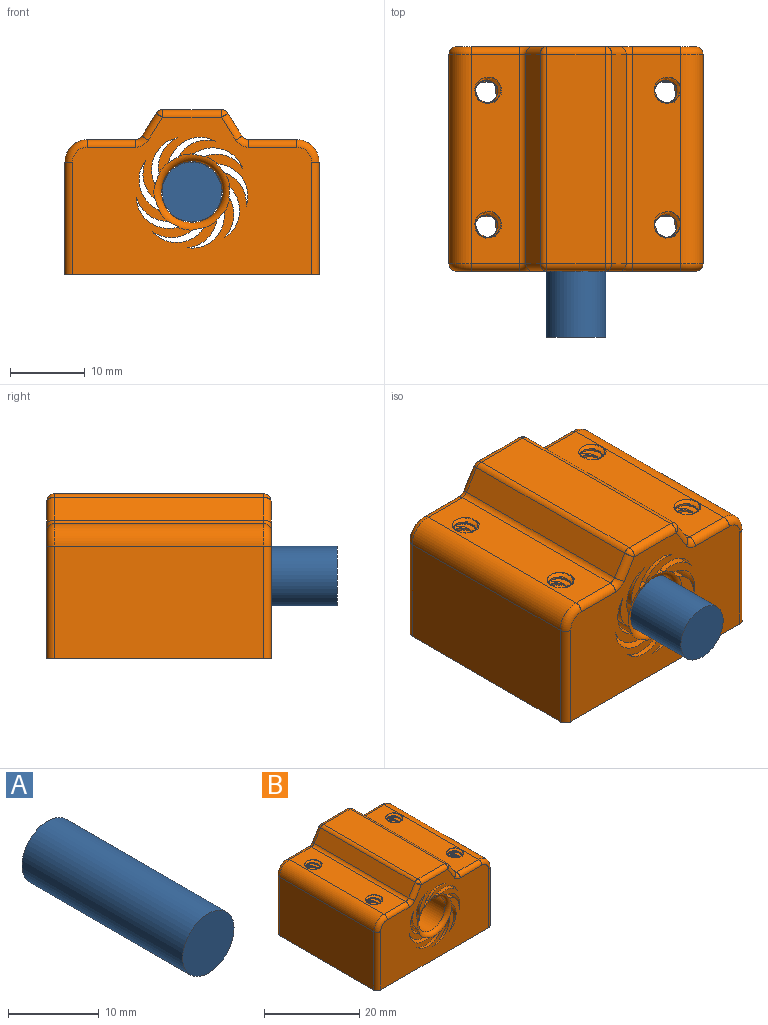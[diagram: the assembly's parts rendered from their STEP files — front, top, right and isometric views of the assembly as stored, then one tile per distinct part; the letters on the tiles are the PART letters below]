
ASSEMBLY  parts=2 mates=1
PART A: 3 faces, bbox 8x25x8 mm
  f0: cylinder r=4mm len=25mm, axis (0,1,0), area 628.3mm2, adj f1,f2
  f1: plane 8x8mm, normal (0,-1,0), area 50.3mm2, adj f0
  f2: plane 8x8mm, normal (0,1,0), area 50.3mm2, adj f0
PART B: 97 faces, bbox 34.8x30.3x22.7 mm
  f0: plane 32x21mm, normal (0,1,0), area 465.1mm2, adj f21,f28,f29,f31,f33,f36,f41,f42
  f1: plane 32x21mm, normal (0,-1,0), area 465.1mm2, adj f21,f30,f32,f34,f37,f39,f46,f52
  f2: plane 28x7.89mm, normal (0,0,1), area 221mm2, adj f40,f41,f46,f47
  f3: bspline ~18.65x4.71mm, area 125.6mm2, adj f5,f6,f21,f24
  f4: bspline ~18.81x4.71mm, area 125.4mm2, adj f5,f6,f21,f24
  f5: bspline ~18.46x4.82mm, area 33.9mm2, adj f3,f4,f21,f24
  f6: cylinder r=1.5mm len=18mm, axis (0,0,1), area 24.7mm2, adj f3,f4,f21,f24
  f7: bspline ~18.65x4.71mm, area 125.6mm2, adj f9,f10,f21,f24
  f8: bspline ~18.81x4.71mm, area 125.4mm2, adj f9,f10,f21,f24
  f9: bspline ~18.46x4.82mm, area 33.9mm2, adj f7,f8,f21,f24
  f10: cylinder r=1.5mm len=18mm, axis (0,0,1), area 24.7mm2, adj f7,f8,f21,f24
  f11: bspline ~18.65x4.71mm, area 125.6mm2, adj f13,f14,f21,f22
  f12: bspline ~18.81x4.71mm, area 125.4mm2, adj f13,f14,f21,f22
  f13: bspline ~18.46x4.82mm, area 33.9mm2, adj f11,f12,f21,f22
  f14: cylinder r=1.5mm len=18mm, axis (0,0,1), area 24.7mm2, adj f11,f12,f21,f22
  f15: bspline ~18.65x4.71mm, area 125.6mm2, adj f17,f18,f21,f22
  f16: bspline ~18.81x4.71mm, area 125.4mm2, adj f17,f18,f21,f22
  f17: bspline ~18.46x4.82mm, area 33.9mm2, adj f15,f16,f21,f22
  f18: cylinder r=1.5mm len=18mm, axis (0,0,1), area 24.7mm2, adj f15,f16,f21,f22
  f19: plane 28x15mm, normal (-1,0,0), area 420mm2, adj f21,f26,f28,f30
  f20: plane 28x15mm, normal (1,0,0), area 420mm2, adj f21,f27,f42,f55
  f21: plane 34.28x30.28mm, normal (0,0,-1), area 980.6mm2, adj f0,f1,f3,f4,f5,f6,f7,f8
  f22: plane 28.28x6.72mm, normal (0,0,1), area 161.2mm2, adj f11,f12,f13,f14,f15,f16,f17,f18
  f23: plane 28x3.06mm, normal (0.85,0,0.53), area 101mm2, adj f47,f48,f52,f53
  f24: plane 28.28x6.72mm, normal (0,0,1), area 161.2mm2, adj f3,f4,f5,f6,f7,f8,f9,f10
  f25: plane 28x3.06mm, normal (-0.85,0,0.53), area 101mm2, adj f35,f36,f39,f40
  f26: cylinder r=3mm len=28mm, axis (0,-1,0), area 131.9mm2, adj f19,f24,f29,f32
  f27: cylinder r=3mm len=28mm, axis (0,1,0), area 131.9mm2, adj f20,f22,f45,f57
  f28: cylinder r=1mm len=15mm, axis (0,0,-1), area 23.6mm2, adj f0,f19,f21,f29
  f29: torus R=2mm, axis (0,1,0), area 6.5mm2, adj f0,f26,f28,f31
  f30: cylinder r=1mm len=15mm, axis (0,0,1), area 23.6mm2, adj f1,f19,f21,f32
  f31: cylinder r=1mm len=6.45mm, axis (1,0,0), area 10.1mm2, adj f0,f24,f29,f33
  f32: torus R=2mm, axis (0,1,0), area 6.5mm2, adj f1,f26,f30,f34
  f33: torus R=2mm, axis (0,1,0), area 2.2mm2, adj f0,f31,f35,f36
  f34: cylinder r=1mm len=6.45mm, axis (1,0,0), area 10.1mm2, adj f1,f24,f32,f37
  f35: cylinder r=1mm len=28mm, axis (0,1,0), area 28.3mm2, adj f24,f25,f33,f37
  f36: cylinder r=1mm len=3.59mm, axis (0.53,0,0.85), area 5.7mm2, adj f0,f25,f33,f38
  f37: torus R=2mm, axis (0,1,0), area 2.2mm2, adj f1,f34,f35,f39
  f38: sphere r=1mm, area 1.1mm2, adj f36,f40,f41
  f39: cylinder r=1mm len=3.59mm, axis (0.53,0,0.85), area 5.7mm2, adj f1,f25,f37,f43
  f40: cylinder r=1mm len=28mm, axis (0,-1,0), area 28.3mm2, adj f2,f25,f38,f43
  f41: cylinder r=1mm len=7.89mm, axis (1,0,0), area 12.4mm2, adj f0,f2,f38,f44
  f42: cylinder r=1mm len=15mm, axis (0,0,1), area 23.6mm2, adj f0,f20,f21,f45
  f43: sphere r=1mm, area 1.1mm2, adj f39,f40,f46
  f44: sphere r=1mm, area 1.1mm2, adj f41,f47,f48
  f45: torus R=2mm, axis (0,1,0), area 6.5mm2, adj f0,f27,f42,f49
  f46: cylinder r=1mm len=7.89mm, axis (-1,0,0), area 12.4mm2, adj f1,f2,f43,f50
  f47: cylinder r=1mm len=28mm, axis (0,1,0), area 28.3mm2, adj f2,f23,f44,f50
  f48: cylinder r=1mm len=3.59mm, axis (0.53,0,-0.85), area 5.7mm2, adj f0,f23,f44,f51
  f49: cylinder r=1mm len=6.45mm, axis (1,0,0), area 10.1mm2, adj f0,f22,f45,f51
  f50: sphere r=1mm, area 1mm2, adj f46,f47,f52
  f51: torus R=2mm, axis (0,1,0), area 2.2mm2, adj f0,f48,f49,f53
  f52: cylinder r=1mm len=3.59mm, axis (0.53,0,-0.85), area 5.7mm2, adj f1,f23,f50,f54
  f53: cylinder r=1mm len=28mm, axis (0,-1,0), area 28.3mm2, adj f22,f23,f51,f54
  f54: torus R=2mm, axis (0,1,0), area 2.2mm2, adj f1,f52,f53,f56
  f55: cylinder r=1mm len=15mm, axis (0,0,-1), area 23.6mm2, adj f1,f20,f21,f57
  f56: cylinder r=1mm len=6.45mm, axis (1,0,0), area 10.1mm2, adj f1,f22,f54,f57
  f57: torus R=2mm, axis (0,1,0), area 6.5mm2, adj f1,f27,f55,f56
  f58: cylinder r=4.1mm len=28mm, axis (0,-1,0), area 721.3mm2, adj f95,f96
  f59: cylinder r=7.5mm len=30mm, axis (0,-1,0), area 45.1mm2, adj f0,f1,f60,f62
  f60: cylinder r=4.42mm len=30mm, axis (0,-1,0), area 195.7mm2, adj f0,f1,f59,f61,f95,f96
  f61: cylinder r=5mm len=29.99mm, axis (0,-1,0), area 45.2mm2, adj f60,f62,f95,f96
  f62: cylinder r=4.42mm len=30mm, axis (0,-1,0), area 175.9mm2, adj f0,f1,f59,f61,f95,f96
  f63: cylinder r=7.5mm len=30mm, axis (0,-1,0), area 45.1mm2, adj f0,f1,f64,f66
  f64: cylinder r=4.42mm len=30mm, axis (0,-1,0), area 195.7mm2, adj f0,f1,f63,f65,f95,f96
  f65: cylinder r=5mm len=29.99mm, axis (0,-1,0), area 45.2mm2, adj f64,f66,f95,f96
  f66: cylinder r=4.42mm len=30mm, axis (0,-1,0), area 175.9mm2, adj f0,f1,f63,f65,f95,f96
  f67: cylinder r=7.5mm len=30mm, axis (0,-1,0), area 45.1mm2, adj f0,f1,f68,f70
  f68: cylinder r=4.42mm len=30mm, axis (0,-1,0), area 195.7mm2, adj f0,f1,f67,f69,f95,f96
  f69: cylinder r=5mm len=29.99mm, axis (0,-1,0), area 45.2mm2, adj f68,f70,f95,f96
  f70: cylinder r=4.42mm len=30mm, axis (0,-1,0), area 175.9mm2, adj f0,f1,f67,f69,f95,f96
  f71: cylinder r=4.42mm len=30mm, axis (0,-1,0), area 195.7mm2, adj f0,f1,f72,f74,f95,f96
  f72: cylinder r=5mm len=29.99mm, axis (0,-1,0), area 45.2mm2, adj f71,f73,f95,f96
  f73: cylinder r=4.42mm len=30mm, axis (0,-1,0), area 175.9mm2, adj f0,f1,f72,f74,f95,f96
  f74: cylinder r=7.5mm len=30mm, axis (0,-1,0), area 45.1mm2, adj f0,f1,f71,f73
  f75: cylinder r=7.5mm len=30mm, axis (0,-1,0), area 45.1mm2, adj f0,f1,f76,f78
  f76: cylinder r=4.42mm len=30mm, axis (0,-1,0), area 195.7mm2, adj f0,f1,f75,f77,f95,f96
  f77: cylinder r=5mm len=29.99mm, axis (0,-1,0), area 45.2mm2, adj f76,f78,f95,f96
  f78: cylinder r=4.42mm len=30mm, axis (0,-1,0), area 175.9mm2, adj f0,f1,f75,f77,f95,f96
  f79: cylinder r=7.5mm len=30mm, axis (0,-1,0), area 45.1mm2, adj f0,f1,f80,f82
  f80: cylinder r=4.42mm len=30mm, axis (0,-1,0), area 195.7mm2, adj f0,f1,f79,f81,f95,f96
  f81: cylinder r=5mm len=29.99mm, axis (0,-1,0), area 45.2mm2, adj f80,f82,f95,f96
  f82: cylinder r=4.42mm len=30mm, axis (0,-1,0), area 175.9mm2, adj f0,f1,f79,f81,f95,f96
  f83: cylinder r=7.5mm len=30mm, axis (0,-1,0), area 45.1mm2, adj f0,f1,f84,f86
  f84: cylinder r=4.42mm len=30mm, axis (0,-1,0), area 195.7mm2, adj f0,f1,f83,f85,f95,f96
  f85: cylinder r=5mm len=29.99mm, axis (0,-1,0), area 45.2mm2, adj f84,f86,f95,f96
  f86: cylinder r=4.42mm len=30mm, axis (0,-1,0), area 175.9mm2, adj f0,f1,f83,f85,f95,f96
  f87: cylinder r=7.5mm len=30mm, axis (0,-1,0), area 45.1mm2, adj f0,f1,f88,f90
  f88: cylinder r=4.42mm len=30mm, axis (0,-1,0), area 195.7mm2, adj f0,f1,f87,f89,f95,f96
  f89: cylinder r=5mm len=29.99mm, axis (0,-1,0), area 45.2mm2, adj f88,f90,f95,f96
  f90: cylinder r=4.42mm len=30mm, axis (0,-1,0), area 175.9mm2, adj f0,f1,f87,f89,f95,f96
  f91: cylinder r=7.5mm len=30mm, axis (0,-1,0), area 45.1mm2, adj f0,f1,f92,f94
  f92: cylinder r=4.42mm len=30mm, axis (0,-1,0), area 195.7mm2, adj f0,f1,f91,f93,f95,f96
  f93: cylinder r=5mm len=29.99mm, axis (0,-1,0), area 45.2mm2, adj f92,f94,f95,f96
  f94: cylinder r=4.42mm len=30mm, axis (0,-1,0), area 175.9mm2, adj f0,f1,f91,f93,f95,f96
  f95: torus R=5.1mm, axis (0,1,0), area 42.7mm2, adj f1,f58,f60,f61,f62,f64,f65,f66
  f96: torus R=5.1mm, axis (0,1,0), area 42.7mm2, adj f0,f58,f60,f61,f62,f64,f65,f66
PLACE A t=(29.55,9.63,28.9)mm
PLACE B t=(12.55,-6.52,17.9)mm
MATE slider B.f58 <-> A.f0  axis (0,-1,0) through (29.55,8.48,28.9)mm
